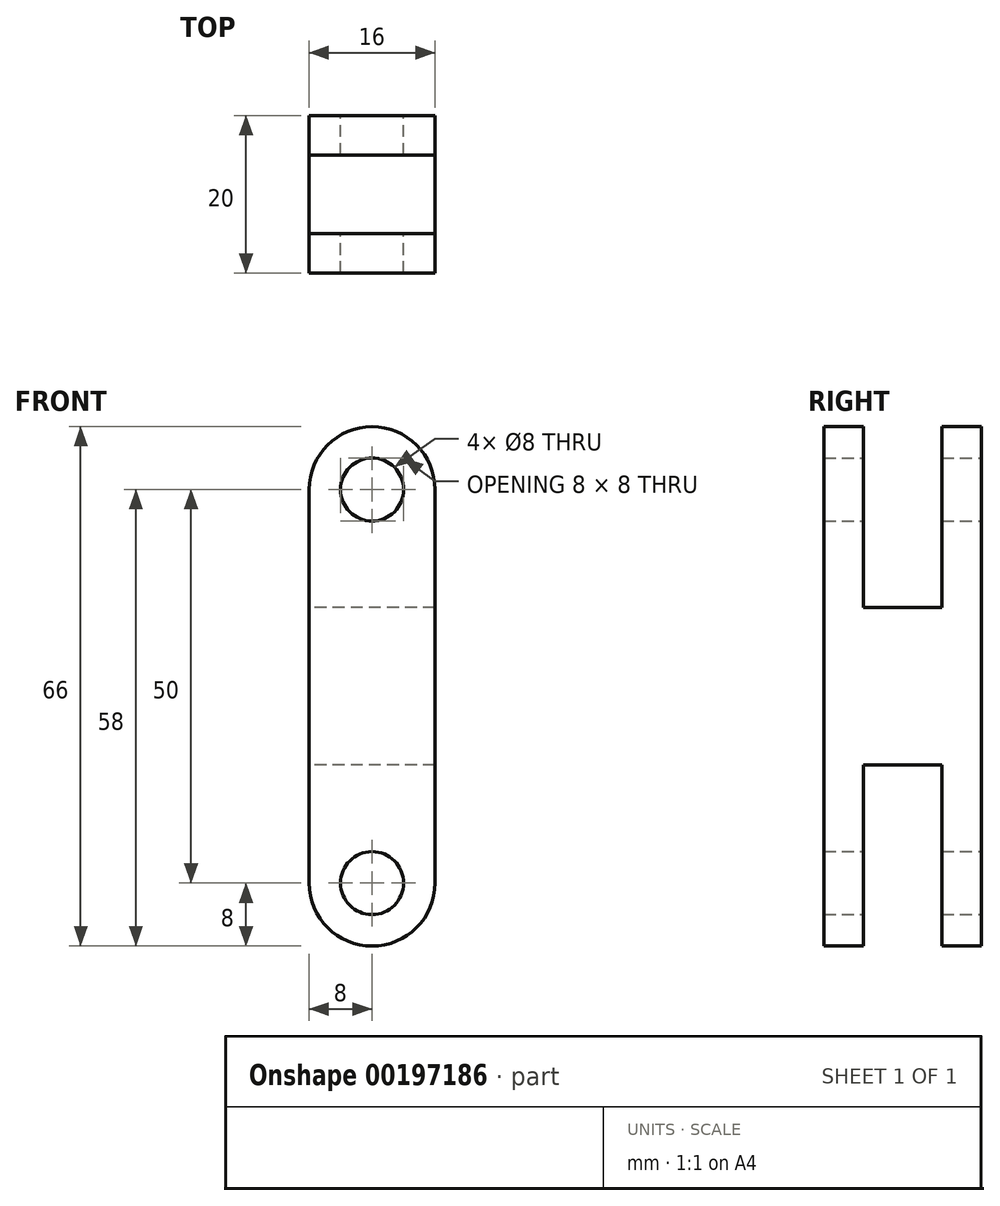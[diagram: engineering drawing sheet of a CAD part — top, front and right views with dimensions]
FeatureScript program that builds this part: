
annotation { "Feature Type Name" : "Feature", "Feature Type Description" : "" }
export const myFeature = defineFeature(function(context is Context, id is Id, definition is map)
    precondition{}
    {
        {
            var Q0;
            Q0=qCreatedBy(makeId("Front.planeOp"),FACE);
            var sketch = newSketch(context, id + "F0", { "sketchPlane" : qUnion([Q0])});
            skLineSegment(sketch, "E0", {"start": v(0, -25) * mm, "end": v(0, 25) * mm, "construction": true});
            skArc(sketch, "E1", {"start": v(8, 25) * mm, "mid": v(0, 33) * mm, "end": v(-8, 25) * mm});
            skArc(sketch, "E2", {"start": v(-8, -25) * mm, "mid": v(0, -33) * mm, "end": v(8, -25) * mm});
            skLineSegment(sketch, "E3", {"start": v(-8, -25) * mm, "end": v(-8, 25) * mm});
            skLineSegment(sketch, "E4", {"start": v(8, -25) * mm, "end": v(8, 25) * mm});
            skCircle(sketch, "E5", {"center": v(0, 25) * mm, "radius": 4 * mm});
            skCircle(sketch, "E6", {"center": v(0, -25) * mm, "radius": 4 * mm});
            skSolve(sketch);
        }
        {
            var Q0;
            Q0 = qSketchRegion(id + "F0", true);
            extrude(context, id + "F1", {"entities" : qUnion([Q0]), "depth" : 20 * mm});
        }
        {
            var Q0;
            Q0=makeQuery(id+"F1.opExtrude","SWEPT_FACE",FACE,{"disambiguationData":[OSD([sQuery(id+"F0.wireOp",EDGE,"E3")])]});
            var sketch = newSketch(context, id + "F2", { "sketchPlane" : qUnion([Q0])});
            skLineSegment(sketch, "E7.bottom", {"start": v(5, 45) * mm, "end": v(15, 45) * mm});
            skLineSegment(sketch, "E7.top", {"start": v(5, 10) * mm, "end": v(15, 10) * mm});
            skLineSegment(sketch, "E7.left", {"start": v(5, 45) * mm, "end": v(5, 10) * mm});
            skLineSegment(sketch, "E7.right", {"start": v(15, 45) * mm, "end": v(15, 10) * mm});
            skLineSegment(sketch, "E8", {"start": v(0, 0) * mm, "end": v(20, 0) * mm, "construction": true});
            skLineSegment(sketch, "E9", {"start": v(10, 0) * mm, "end": v(10, 45) * mm, "construction": true});
            skLineSegment(sketch, "E10.MirrorCS", {"start": v(5, -10) * mm, "end": v(15, -10) * mm});
            skLineSegment(sketch, "E11.MirrorCS", {"start": v(15, -45) * mm, "end": v(15, -10) * mm});
            skLineSegment(sketch, "E12.MirrorCS", {"start": v(5, -45) * mm, "end": v(5, -10) * mm});
            skLineSegment(sketch, "E13.MirrorCS", {"start": v(5, -45) * mm, "end": v(15, -45) * mm});
            skSolve(sketch);
        }
        {
            var Q0;
            Q0 = qSketchRegion(id + "F2", true);
            extrude(context, id + "F3", {"entities" : qUnion([Q0]), "operationType" : NewBodyOperationType.REMOVE, "endBound" : BoundingType.THROUGH_ALL, "oppositeDirection" : true, "depth" : 25 * mm});
        }
    });
